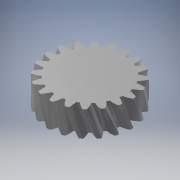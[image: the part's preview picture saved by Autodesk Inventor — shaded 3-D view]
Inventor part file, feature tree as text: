
AUTODESK INVENTOR PART (.ipt)
format: ipt  version: 2017 SP1 (Build 210196100, 196)  size: 418,304 bytes
history: native  units: mm (DEFAULTED — no unit token found)
features: plane x3, other x3, sketch x2, extrude x1
ambient origin geometry x8: Origin, YZ Plane, XZ Plane, XY Plane, X Axis, Y Axis, Z Axis, Center Point
bodies: Solid1 (feature_tree)
feature tree (9):
  extrude  "Extrusion1"  Depth=10.0mm TaperAngle=0.0deg
  plane  "Work Plane2"
  plane  "Work Plane8"
  plane  "Work Plane9"
  other  "Engrenage cylindrique"
  sketch  "Sketch1"  dims[d0=32.749068mm d1=10.0mm d2=0.0mm]
  sketch  "Sketch2"  dims[d3=30.066593mm d4=10.0mm d5=0.0mm d16=30.066593mm d17=0.0mm d34=1.570796mm d39=0.0mm d41=0.0mm d43=30.066593mm d46=30.066593mm d47=0.0mm d48=0.0mm]
  other  "Srf1"
  other  "Diamètre primitif"
